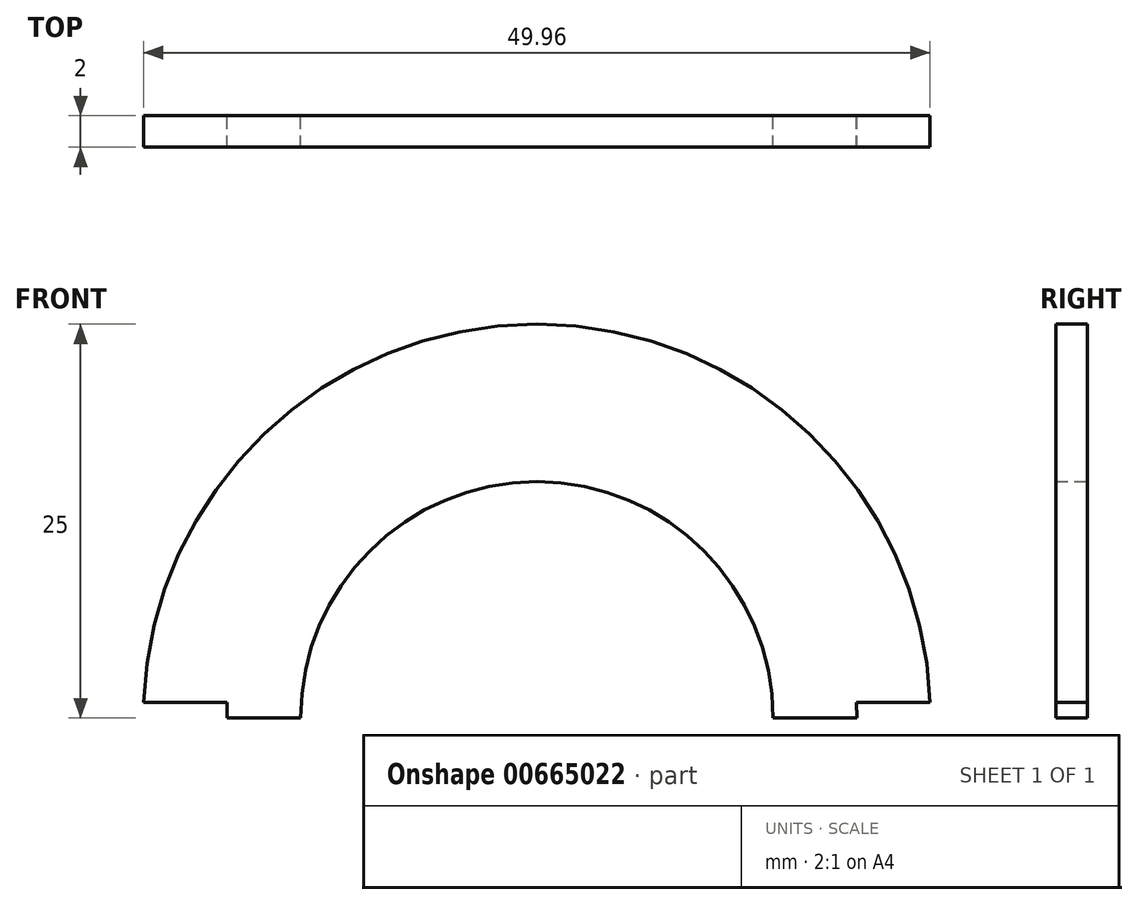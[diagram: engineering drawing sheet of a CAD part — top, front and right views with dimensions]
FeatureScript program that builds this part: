
annotation { "Feature Type Name" : "Feature", "Feature Type Description" : "" }
export const myFeature = defineFeature(function(context is Context, id is Id, definition is map)
    precondition{}
    {
        {
            var Q0;
            Q0=qCreatedBy(makeId("Front.planeOp"),FACE);
            var sketch = newSketch(context, id + "F0", { "sketchPlane" : qUnion([Q0])});
            skArc(sketch, "E0", {"start": v(0, 15) * mm, "mid": v(-10.6, 10.6) * mm, "end": v(-15, 0) * mm});
            skArc(sketch, "E1", {"start": v(15, 0) * mm, "mid": v(10.6, 10.6) * mm, "end": v(0, 15) * mm});
            skCircle(sketch, "E2", {"center": v(0.3, 0) * mm, "radius": 20 * mm, "construction": true});
            skArc(sketch, "E3", {"start": v(0, 25) * mm, "mid": v(-17.33, 18.02) * mm, "end": v(-24.98, 0.98) * mm});
            skLineSegment(sketch, "E4", {"start": v(-24.98, 0.98) * mm, "end": v(-19.67, 0.98) * mm});
            skLineSegment(sketch, "E5", {"start": v(-19.67, 0.98) * mm, "end": v(-19.67, 0) * mm});
            skArc(sketch, "E6", {"start": v(24.98, 0.98) * mm, "mid": v(17.33, 18.02) * mm, "end": v(0, 25) * mm});
            skLineSegment(sketch, "E7", {"start": v(-19.67, 0) * mm, "end": v(-15, 0) * mm});
            skLineSegment(sketch, "E8", {"start": v(24.98, 0.98) * mm, "end": v(20.29, 0.98) * mm});
            skLineSegment(sketch, "E9", {"start": v(20.29, 0.98) * mm, "end": v(20.33, 0) * mm});
            skLineSegment(sketch, "E10", {"start": v(15, 0) * mm, "end": v(20.33, 0) * mm});
            skSolve(sketch);
        }
        {
            var Q0;
            Q0 = qSketchRegion(id + "F0", true);
            extrude(context, id + "F1", {"entities" : qUnion([Q0]), "depth" : 2 * mm, "offsetDistance" : 25 * mm});
        }
        {
            var Q0;
            Q0 = qSketchRegion(id + "F0", true);
            extrude(context, id + "F2", {"entities" : qUnion([Q0]), "operationType" : NewBodyOperationType.ADD, "depth" : 2 * mm, "offsetDistance" : 25 * mm});
        }
    });
